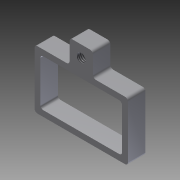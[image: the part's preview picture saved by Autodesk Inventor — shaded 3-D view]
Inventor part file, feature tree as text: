
AUTODESK INVENTOR PART (.ipt)
format: ipt  version: 2011 (Build 150239000, 239)  size: 138,752 bytes
history: native  units: in
note: dims shown in document units (in); Inventor stores cm internally (conversion verified against a paired STEP export)
features: sketch x5, extrude x4, hole x1, thread x1, fillet x1
ambient origin geometry x8: Origin, YZ Plane, XZ Plane, XY Plane, X Axis, Y Axis, Z Axis, Center Point
bodies: Solid1 (feature_tree)
feature tree (12):
  extrude  "Extrusion1"  Depth=0.3937in
  extrude  "Extrusion2"  Depth=0.5512in
  extrude  "Extrusion3"  Depth=0.1181in TaperAngle=0.0deg
  hole  "Hole1"  [1 undecoded]
  thread  "Thread1"  [1 undecoded]
  extrude  "Extrusion5"  Depth=1.0in TaperAngle=0.0deg
  fillet  "Fillet2"  Radius=0.0787in
  sketch  "Sketch1"  dims[d0=0.6299in d1=0.3937in]
  sketch  "Sketch2"  dims[d2=0.1181in d3=0.0in d4=0.5512in]
  sketch  "Sketch3"  dims[d5=0.315in d6=0.1181in d7=0.0in]
  sketch  "Sketch6"  dims[d13=0.1575in d14=0.2362in d15=0.1575in d16=0.0in]
  sketch  "Sketch7"  dims[d20=0.06in d21=0.75in d22=0.375in d23=0.25in d24=0.5635in d25=0.07in d26=0.8108in d27=1.0in d28=0.0in d29=0.0787in d30=0.0394in d31=0.2756in d32=0.0394in d33=0.0in d35=0.0197in]
note: 2 required parameter values undecoded (feature->parameter linkage not recoverable at this tier; creation-order binding heuristic only, values carry confidence <= 0.55)
